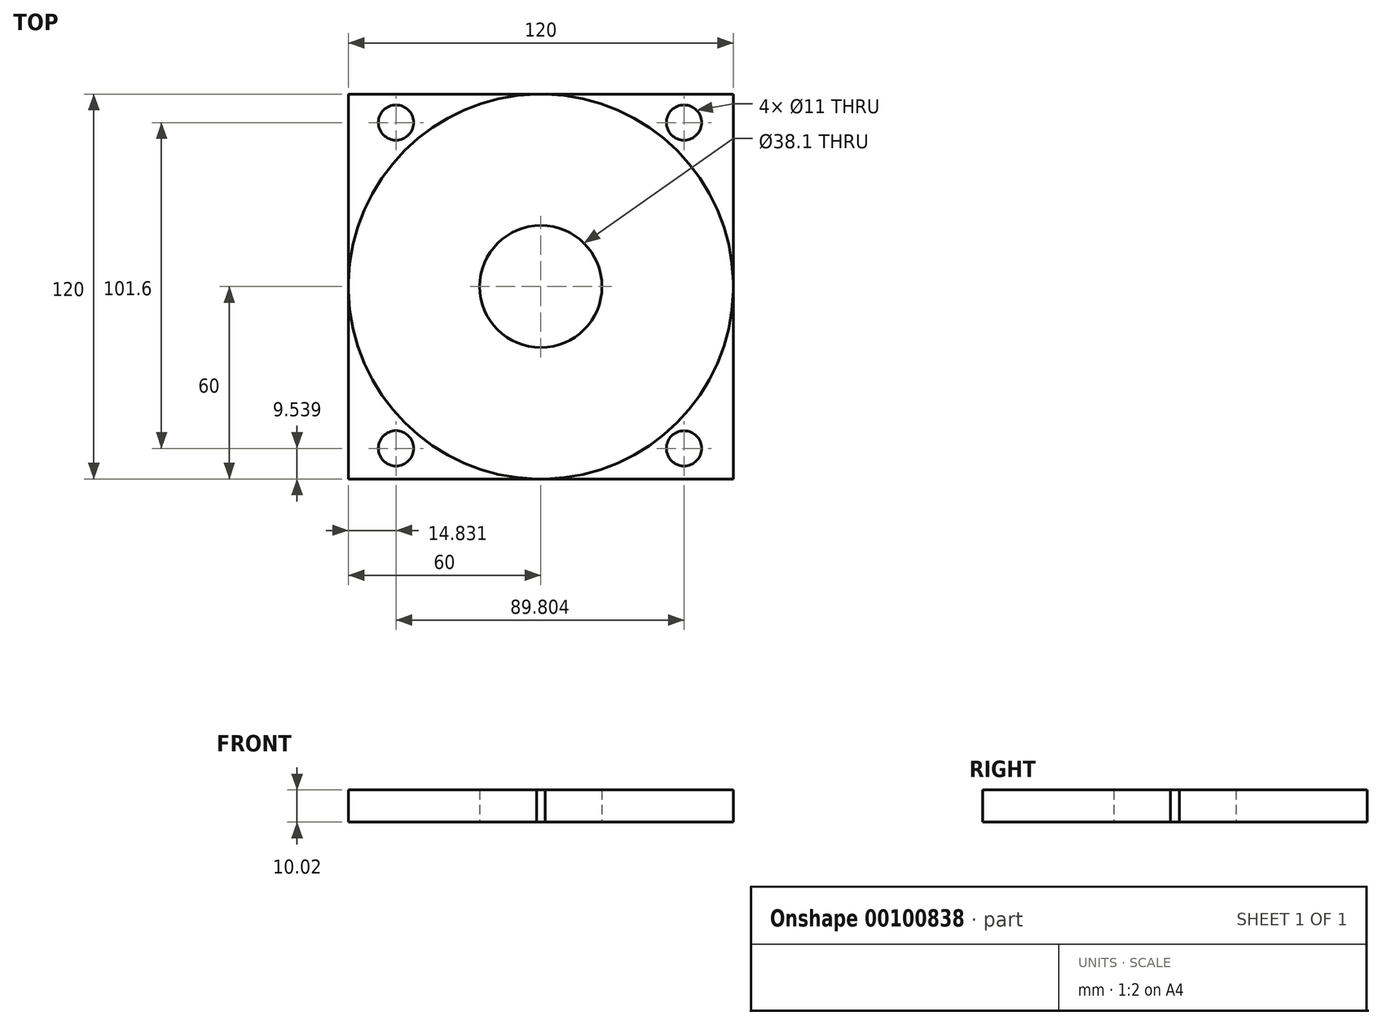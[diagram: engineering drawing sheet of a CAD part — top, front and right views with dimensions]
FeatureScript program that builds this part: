
annotation { "Feature Type Name" : "Feature", "Feature Type Description" : "" }
export const myFeature = defineFeature(function(context is Context, id is Id, definition is map)
    precondition{}
    {
        {
            var Q0;
            Q0=qCreatedBy(makeId("Top.planeOp"),FACE);
            var sketch = newSketch(context, id + "F0", { "sketchPlane" : qUnion([Q0])});
            skLineSegment(sketch, "E0.bottom", {"start": v(-60, 60) * mm, "end": v(60, 60) * mm});
            skLineSegment(sketch, "E0.top", {"start": v(-60, -60) * mm, "end": v(60, -60) * mm});
            skLineSegment(sketch, "E0.left", {"start": v(-60, 60) * mm, "end": v(-60, -60) * mm});
            skLineSegment(sketch, "E0.right", {"start": v(60, 60) * mm, "end": v(60, -60) * mm});
            skLineSegment(sketch, "E1.bottom", {"start": v(60, 0) * mm, "end": v(0, 0) * mm});
            skLineSegment(sketch, "E1.top", {"start": v(60, 60) * mm, "end": v(0, 60) * mm});
            skLineSegment(sketch, "E1.left", {"start": v(60, 0) * mm, "end": v(60, 60) * mm});
            skCircle(sketch, "E2", {"center": v(0, 0) * mm, "radius": 19.05 * mm});
            skCircle(sketch, "E3", {"center": v(-45.17, 51.14) * mm, "radius": 3.5 * mm});
            skCircle(sketch, "E4.0.1.0", {"center": v(-45.17, -50.46) * mm, "radius": 3.5 * mm});
            skCircle(sketch, "E4.1.0.0", {"center": v(44.64, 51.14) * mm, "radius": 3.5 * mm});
            skCircle(sketch, "E4.1.1.0", {"center": v(44.64, -50.46) * mm, "radius": 3.5 * mm});
            skLineSegment(sketch, "E4.direction1", {"start": v(-45.17, 51.14) * mm, "end": v(44.64, 51.14) * mm, "construction": true});
            skLineSegment(sketch, "E4.direction2", {"start": v(-45.17, 51.14) * mm, "end": v(-45.17, -50.46) * mm, "construction": true});
            skSolve(sketch);
        }
        {
            var Q0;
            Q0=makeQuery(id+"F0.imprint","IMPRINT",FACE,{"disambiguationData":[TD([[makeQuery(id+"F0.imprint","IMPRINT",EDGE,{"derivedFrom":sQuery(id+"F0.wireOp",EDGE,"E0.bottom")}),-1.0]])]});
            extrude(context, id + "F1", {"entities" : qUnion([Q0]), "depth" : 7 / 406.4 * mm});
        }
        {
            var Q0;
            Q0=makeQuery(id+"F1.opExtrude","CAP_FACE",FACE,{"disambiguationData":[OSD([sQuery(id+"F0.wireOp",EDGE,"E0.bottom"),sQuery(id+"F0.wireOp",EDGE,"E0.top"),sQuery(id+"F0.wireOp",EDGE,"E0.left"),sQuery(id+"F0.wireOp",EDGE,"E0.right"),sQuery(id+"F0.wireOp",EDGE,"E1.top"),sQuery(id+"F0.wireOp",EDGE,"E1.left"),sQuery(id+"F0.wireOp",EDGE,"E2"),sQuery(id+"F0.wireOp",EDGE,"E3"),sQuery(id+"F0.wireOp",EDGE,"E4.0.1.0"),sQuery(id+"F0.wireOp",EDGE,"E4.1.0.0"),sQuery(id+"F0.wireOp",EDGE,"E4.1.1.0")])],"isStart":false});
            var sketch = newSketch(context, id + "F2", { "sketchPlane" : qUnion([Q0])});
            skCircle(sketch, "E5", {"center": v(-45.17, -50.46) * mm, "radius": 5.5 * mm});
            skCircle(sketch, "E6", {"center": v(44.64, -50.46) * mm, "radius": 5.5 * mm});
            skCircle(sketch, "E7", {"center": v(44.64, 51.14) * mm, "radius": 5.5 * mm});
            skCircle(sketch, "E8", {"center": v(-45.17, 51.14) * mm, "radius": 5.5 * mm});
            skSolve(sketch);
        }
        {
            var Q0;
            Q0 = qSketchRegion(id + "F2", true);
            extrude(context, id + "F3", {"entities" : qUnion([Q0]), "operationType" : NewBodyOperationType.REMOVE, "oppositeDirection" : true, "depth" : 9 * mm});
        }
        {
            var Q0;
            Q0=makeQuery(id+"F1.opExtrude","CAP_FACE",FACE,{"disambiguationData":[OSD([sQuery(id+"F0.wireOp",EDGE,"E0.bottom"),sQuery(id+"F0.wireOp",EDGE,"E0.top"),sQuery(id+"F0.wireOp",EDGE,"E0.left"),sQuery(id+"F0.wireOp",EDGE,"E0.right"),sQuery(id+"F0.wireOp",EDGE,"E1.top"),sQuery(id+"F0.wireOp",EDGE,"E1.left"),sQuery(id+"F0.wireOp",EDGE,"E2"),sQuery(id+"F0.wireOp",EDGE,"E3"),sQuery(id+"F0.wireOp",EDGE,"E4.0.1.0"),sQuery(id+"F0.wireOp",EDGE,"E4.1.0.0"),sQuery(id+"F0.wireOp",EDGE,"E4.1.1.0")])],"isStart":false});
            var sketch = newSketch(context, id + "F4", { "sketchPlane" : qUnion([Q0])});
            skCircle(sketch, "E9", {"center": v(0, 0) * mm, "radius": 60.02 * mm});
            skSolve(sketch);
        }
        {
            var Q0;
            Q0=makeQuery(id+"F4.imprint","IMPRINT",FACE,{"disambiguationData":[TD([[makeQuery(id+"F4.imprint","IMPRINT",EDGE,{"derivedFrom":makeQuery(id+"F1.opExtrude","CAP_EDGE",EDGE,{"disambiguationData":[OSD([sQuery(id+"F0.wireOp",EDGE,"E2")])],"isStart":false})}),-1.0]])]});
            extrude(context, id + "F5", {"entities" : qUnion([Q0]), "operationType" : NewBodyOperationType.ADD, "depth" : 10 * mm});
        }
    });
